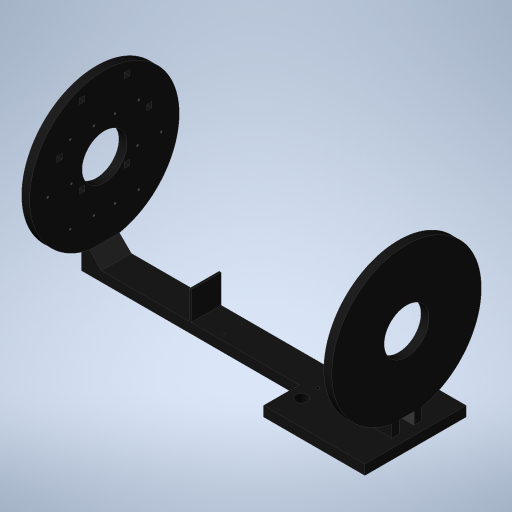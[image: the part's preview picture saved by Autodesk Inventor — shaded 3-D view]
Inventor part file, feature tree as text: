
AUTODESK INVENTOR PART (.ipt)
format: ipt  version: 2023 (Build 270158000, 158)  size: 578,048 bytes
history: native  units: in
note: dims shown in document units (in); Inventor stores cm internally (conversion verified against a paired STEP export)
features: extrude x14, sketch x7, projected_geometry x2, pattern_linear x1
ambient origin geometry x8: Origin, YZ Plane, XZ Plane, XY Plane, X Axis, Y Axis, Z Axis, Center Point
bodies: Solid1 (feature_tree)
feature tree (24):
  extrude  "Extrusion1"  Depth=0.2047in
  extrude  "Extrusion2"  Depth=0.2047in TaperAngle=360.0deg
  extrude  "Extrusion3"  Depth=0.315in
  sketch  "Sketch2"  dims[d31=0.2047in d32=2.3622in d34=360.0deg]
  extrude  "Extrusion4"  Depth=0.2047in
  extrude  "Extrusion5"  Depth=0.315in
  pattern_linear  "Rectangular Pattern1"  Spacing1=0.8465in  [1 undecoded]
  extrude  "Extrusion7"  Depth=4.3307in
  extrude  "Extrusion8"  Depth=1.1811in
  extrude  "Extrusion9"  Depth=0.5906in
  sketch  "Sketch7"  dims[d40=0.315in d41=0.315in]
  extrude  "Extrusion11"  Depth=0.315in
  extrude  "Extrusion12"  Depth=1.122in
  extrude  "Extrusion13"  Depth=0.3937in
  extrude  "Extrusion14"  Depth=0.315in TaperAngle=0.0deg
  extrude  "Extrusion10"  Depth=0.3937in TaperAngle=0.0deg
  extrude  "Extrusion6"  Depth=12.5984in TaperAngle=0.0deg
  sketch  "Sketch3"  dims[d36=0.315in d37=0.315in]
  projected_geometry  "Projected Loop1"
  sketch  "Sketch4"  dims[d38=0.2047in d39=0.2047in]
  projected_geometry  "Projected Loop2"
  sketch  "Sketch8"  dims[d42=0.2047in]
  sketch  "Sketch9"  dims[d43=0.2047in d44=0.8465in d45=4.3307in d46=2.7559in d47=0.5906in d49=0.315in d50=1.122in d51=0.3937in d52=0.315in d53=0.0in d54=0.3937in d55=0.0in d56=12.5984in d57=0.0in d58=4.0in d59=4.0in d60=0.4724in d63=0.2559in d65=4.0157in d66=1.0039in d67=0.3346in d68=0.1181in d69=0.7874in d71=3.7402in d72=0.3937in d74=0.3937in d76=0.3937in d77=0.0in d78=0.3937in d79=0.0in d80=1.0in d81=0.5in d82=3.0118in d83=0.3937in d84=0.0in d85=0.7874in d87=11.9291in d88=0.122in d89=0.0in d90=0.122in d91=0.0in d92=0.0787in d93=1.5157in d94=0.0in d95=2.3622in d97=360.0deg d99=120.0deg d102=120.0deg d105=120.0deg d108=1.7717in d109=5.9055in d110=0.315in d111=0.0in d112=1.7717in d113=5.9055in d114=0.3937in d115=0.0in d116=0.2717in d117=0.0in d118=0.9843in d119=0.7283in d120=0.0827in d122=0.5413in d123=2.3622in d125=360.0deg d127=0.0827in d128=0.5413in d129=0.0827in d130=0.5413in d131=0.0787in d132=45.0deg d133=45.0deg d134=1.1811in d135=0.0in d136=0.2953in d137=0.2953in d138=1.1811in d139=0.0in]
  sketch  "Sketch1"  dims[d8=1.378in d9=1.7717in d12=1.1811in d13=0.315in d14=0.315in d22=1.1811in d23=0.315in d24=1.1811in d25=1.378in d26=1.378in d27=0.1575in d30=0.2047in]
note: 1 required parameter value undecoded (feature->parameter linkage not recoverable at this tier; creation-order binding heuristic only, values carry confidence <= 0.55)
